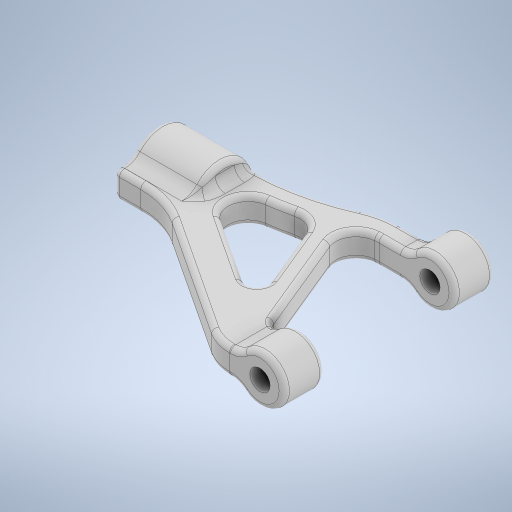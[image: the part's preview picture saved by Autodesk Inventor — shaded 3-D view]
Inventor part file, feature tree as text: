
AUTODESK INVENTOR PART (.ipt)
format: ipt  version: 2024 (Build 280153000, 153)  size: 766,976 bytes
history: native  units: in
note: dims shown in document units (in); Inventor stores cm internally (conversion verified against a paired STEP export)
features: fillet x11, sketch x8, extrude x6, projected_geometry x3, hole x2, other x2, plane x1, direct_edit x1
ambient origin geometry x8: Origin, YZ Plane, XZ Plane, XY Plane, X Axis, Y Axis, Z Axis, Center Point
bodies: Solid1 (feature_tree)
feature tree (34):
  extrude  "Extrusion1"  Depth=0.25in TaperAngle=0.0deg
  plane  "Work Plane1"
  extrude  "Extrusion2"  Depth=0.3in
  extrude  "Extrusion3"  Depth=0.867in
  extrude  "Extrusion4"  Depth=0.425in
  fillet  "Fillet1"  Radius=0.158in
  fillet  "Fillet2"  Radius=1.5in
  extrude  "Extrusion5"  Depth=0.125in
  extrude  "Extrusion6"  Depth=0.125in
  fillet  "Fillet3"  Radius=0.315in
  fillet  "Fillet4"  Radius=0.135in
  fillet  "Fillet5"  Radius=0.5in
  fillet  "Fillet6"  Radius=0.287in
  fillet  "Fillet7"  Radius=0.039in
  fillet  "Fillet8"  Radius=0.039in
  fillet  "Fillet9"  Radius=0.287in
  fillet  "Fillet10"  Radius=0.9546in
  fillet  "Fillet11"  Radius=0.365in
  hole  "Hole1"  [1 undecoded]
  other  "Work Axis1"
  hole  "Hole2"  [1 undecoded]
  direct_edit  "Direct Edit1"
  sketch  "Sketch1"  dims[d0=0.3in d1=0.25in d2=0.0in]
  sketch  "Sketch2"  dims[d3=0.8in d4=0.3in]
  sketch  "Sketch3"  dims[d5=0.25in d6=0.0in d7=0.867in]
  sketch  "Sketch4"  dims[d8=0.425in d9=0.425in d10=0.158in d11=1.5in]
  sketch  "Sketch5"  dims[d12=0.163in d13=0.125in]
  sketch  "Sketch6"  dims[d14=0.189in d15=0.125in d16=0.315in d17=0.135in d18=0.5in d19=0.287in d20=0.039in d21=0.039in d22=0.287in d23=0.9546in d24=0.365in]
  sketch  "Sketch8"  dims[d25=1.52in d26=1.385in]
  sketch  "Sketch9"  dims[d27=0.1625in d28=0.0in d29=0.154in d30=0.125in d31=0.1625in d32=0.0in d33=0.125in d34=0.0625in d35=0.063in d36=1.0in d37=0.0in d38=0.1575in d39=0.375in d40=0.415in d41=0.0in d42=0.15in d43=0.125in d44=0.032in d45=0.032in d46=0.032in d47=0.0625in d48=0.032in d49=0.032in d50=0.0625in d51=0.032in d52=0.134in d53=0.328in d54=0.375in d55=0.25in d56=0.5635in d57=0.375in d58=0.8108in d59=0.125in d60=0.328in d61=0.375in d62=0.25in d63=0.5635in d64=0.375in d65=0.0in d67=3.937in d68=0.3937in d69=0.3937in]
  projected_geometry  "Project Cut Edges1"
  projected_geometry  "Project Cut Edges2"
  projected_geometry  "Project Cut Edges3"
  other  "Scale1"
note: 2 required parameter values undecoded (feature->parameter linkage not recoverable at this tier; creation-order binding heuristic only, values carry confidence <= 0.55)
